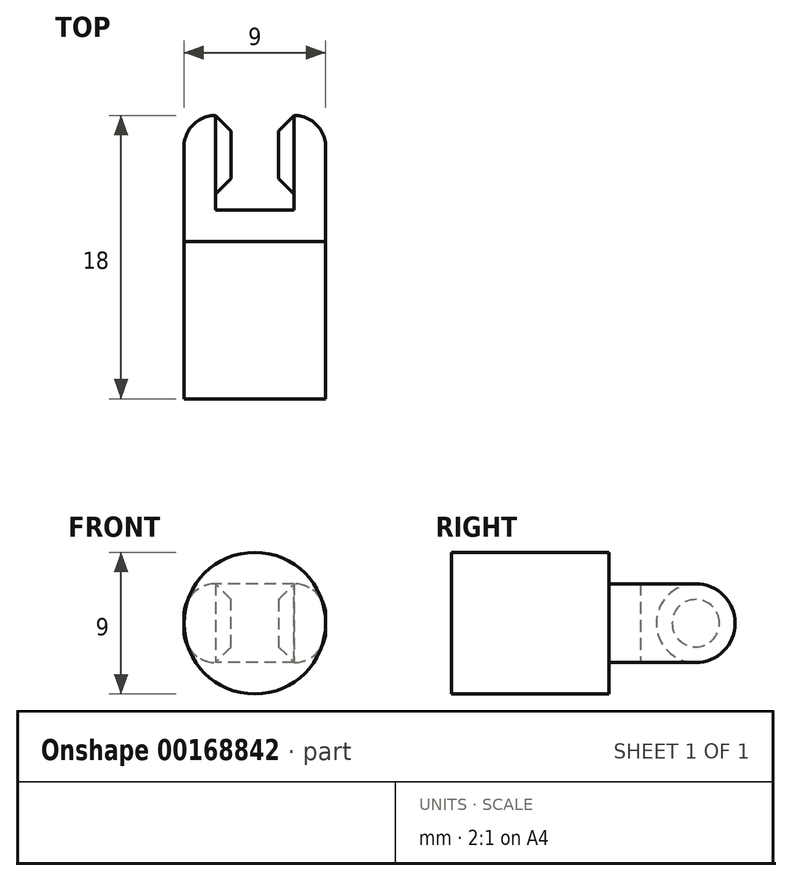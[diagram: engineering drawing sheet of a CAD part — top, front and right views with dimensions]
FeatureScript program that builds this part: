
annotation { "Feature Type Name" : "Feature", "Feature Type Description" : "" }
export const myFeature = defineFeature(function(context is Context, id is Id, definition is map)
    precondition{}
    {
        {
            var Q0;
            Q0=qCreatedBy(makeId("Top.planeOp"),FACE);
            var sketch = newSketch(context, id + "F0", { "sketchPlane" : qUnion([Q0])});
            skLineSegment(sketch, "E0", {"start": v(10.45, 4.27) * mm, "end": v(10.45, 10.27) * mm});
            skLineSegment(sketch, "E1", {"start": v(10.45, 10.27) * mm, "end": v(8.45, 10.27) * mm});
            skLineSegment(sketch, "E2", {"start": v(8.45, 10.27) * mm, "end": v(8.45, 2.27) * mm});
            skLineSegment(sketch, "E3", {"start": v(8.45, 2.27) * mm, "end": v(17.45, 2.27) * mm});
            skLineSegment(sketch, "E4", {"start": v(17.45, 2.27) * mm, "end": v(17.45, 10.27) * mm});
            skLineSegment(sketch, "E5", {"start": v(17.45, 10.27) * mm, "end": v(15.45, 10.27) * mm});
            skLineSegment(sketch, "E6", {"start": v(15.45, 10.27) * mm, "end": v(15.45, 4.27) * mm});
            skLineSegment(sketch, "E7", {"start": v(15.45, 4.27) * mm, "end": v(10.45, 4.27) * mm});
            skSolve(sketch);
        }
        {
            var Q0;
            Q0 = qSketchRegion(id + "F0", true);
            extrude(context, id + "F1", {"entities" : qUnion([Q0]), "depth" : 5 * mm});
        }
        {
            var Q0;
            Q0=makeQuery(id+"F1.opExtrude","SWEPT_FACE",FACE,{"disambiguationData":[OSD([sQuery(id+"F0.wireOp",EDGE,"E0")])]});
            var sketch = newSketch(context, id + "F2", { "sketchPlane" : qUnion([Q0])});
            skCircle(sketch, "E8", {"center": v(7.77, 2.5) * mm, "radius": 2.5 * mm});
            skPoint(sketch, "E8.centerSnap0", {"position": v(10.27, 2.5) * mm});
            skPoint(sketch, "E8.centerSnap1", {"position": v(7.77, 5) * mm});
            skSolve(sketch);
        }
        {
            var Q0;
            Q0 = qSketchRegion(id + "F2", true);
            extrude(context, id + "F3", {"entities" : qUnion([Q0]), "operationType" : NewBodyOperationType.ADD, "depth" : 1 * mm});
        }
        {
            var Q0;
            Q0=makeQuery(id+"F3.opExtrude","CAP_EDGE",EDGE,{"disambiguationData":[OSD([sQuery(id+"F2.wireOp",EDGE,"E8")])],"isStart":false});
            chamfer(context, id + "F4", {"entities" : qUnion([Q0]), "width" : 1 * mm, "tangentPropagation" : true});
        }
        {
            var Q0;
            Q0=makeQuery(id+"F1.opExtrude","SWEPT_FACE",FACE,{"disambiguationData":[OSD([sQuery(id+"F0.wireOp",EDGE,"E6")])]});
            var sketch = newSketch(context, id + "F5", { "sketchPlane" : qUnion([Q0])});
            skCircle(sketch, "E9", {"center": v(-7.77, 2.5) * mm, "radius": 2.5 * mm});
            skPoint(sketch, "E9.centerSnap0", {"position": v(-10.27, 2.5) * mm});
            skPoint(sketch, "E9.centerSnap1", {"position": v(-7.77, 5) * mm});
            skSolve(sketch);
        }
        {
            var Q0;
            Q0 = qSketchRegion(id + "F5", true);
            extrude(context, id + "F6", {"entities" : qUnion([Q0]), "operationType" : NewBodyOperationType.ADD, "depth" : 1 * mm});
        }
        {
            var Q0;
            Q0=makeQuery(id+"F6.opExtrude","CAP_EDGE",EDGE,{"disambiguationData":[OSD([sQuery(id+"F5.wireOp",EDGE,"E9")])],"isStart":false});
            chamfer(context, id + "F7", {"entities" : qUnion([Q0]), "width" : 1 * mm, "tangentPropagation" : true});
        }
        {
            var Q0;
            Q0=makeQuery(id+"F1.opExtrude","CAP_EDGE",EDGE,{"disambiguationData":[OSD([sQuery(id+"F0.wireOp",EDGE,"E5")])],"isStart":false});
            var Q1;
            Q1=makeQuery(id+"F1.opExtrude","CAP_EDGE",EDGE,{"disambiguationData":[OSD([sQuery(id+"F0.wireOp",EDGE,"E5")])],"isStart":true});
            var Q2;
            Q2=makeQuery(id+"F1.opExtrude","CAP_EDGE",EDGE,{"disambiguationData":[OSD([sQuery(id+"F0.wireOp",EDGE,"E1")])],"isStart":false});
            var Q3;
            Q3=makeQuery(id+"F1.opExtrude","CAP_EDGE",EDGE,{"disambiguationData":[OSD([sQuery(id+"F0.wireOp",EDGE,"E1")])],"isStart":true});
            fillet(context, id + "F8", {"entities" : qUnion([Q0, Q1, Q2, Q3]), "radius" : 2.5 * mm, "tangentPropagation" : true, "allowEdgeOverflow" : false});
        }
        {
            var Q0;
            Q0=makeQuery(id+"F1.opExtrude","SWEPT_FACE",FACE,{"disambiguationData":[OSD([sQuery(id+"F0.wireOp",EDGE,"E3")])]});
            var sketch = newSketch(context, id + "F9", { "sketchPlane" : qUnion([Q0])});
            skCircle(sketch, "E10", {"center": v(12.95, 2.5) * mm, "radius": 4.5 * mm});
            skPoint(sketch, "E10.centerSnap0", {"position": v(8.45, 2.5) * mm});
            skPoint(sketch, "E10.centerSnap1", {"position": v(12.95, 5) * mm});
            skSolve(sketch);
        }
        {
            var Q0;
            Q0 = qSketchRegion(id + "F9", true);
            extrude(context, id + "F10", {"entities" : qUnion([Q0]), "operationType" : NewBodyOperationType.ADD, "depth" : 10 * mm});
        }
        {
            var Q0;
            Q0=makeQuery(id+"F1.opExtrude","CAP_EDGE",EDGE,{"disambiguationData":[OSD([sQuery(id+"F0.wireOp",EDGE,"E2")])],"isStart":false});
            var Q1;
            Q1=makeQuery(id+"F1.opExtrude","CAP_EDGE",EDGE,{"disambiguationData":[OSD([sQuery(id+"F0.wireOp",EDGE,"E2")])],"isStart":true});
            var Q2;
            Q2=makeQuery(id+"F1.opExtrude","CAP_EDGE",EDGE,{"disambiguationData":[OSD([sQuery(id+"F0.wireOp",EDGE,"E4")])],"isStart":true});
            var Q3;
            Q3=makeQuery(id+"F1.opExtrude","CAP_EDGE",EDGE,{"disambiguationData":[OSD([sQuery(id+"F0.wireOp",EDGE,"E4")])],"isStart":false});
            fillet(context, id + "F11", {"entities" : qUnion([Q0, Q1, Q2, Q3]), "radius" : 2 * mm, "tangentPropagation" : true, "allowEdgeOverflow" : false});
        }
    });
